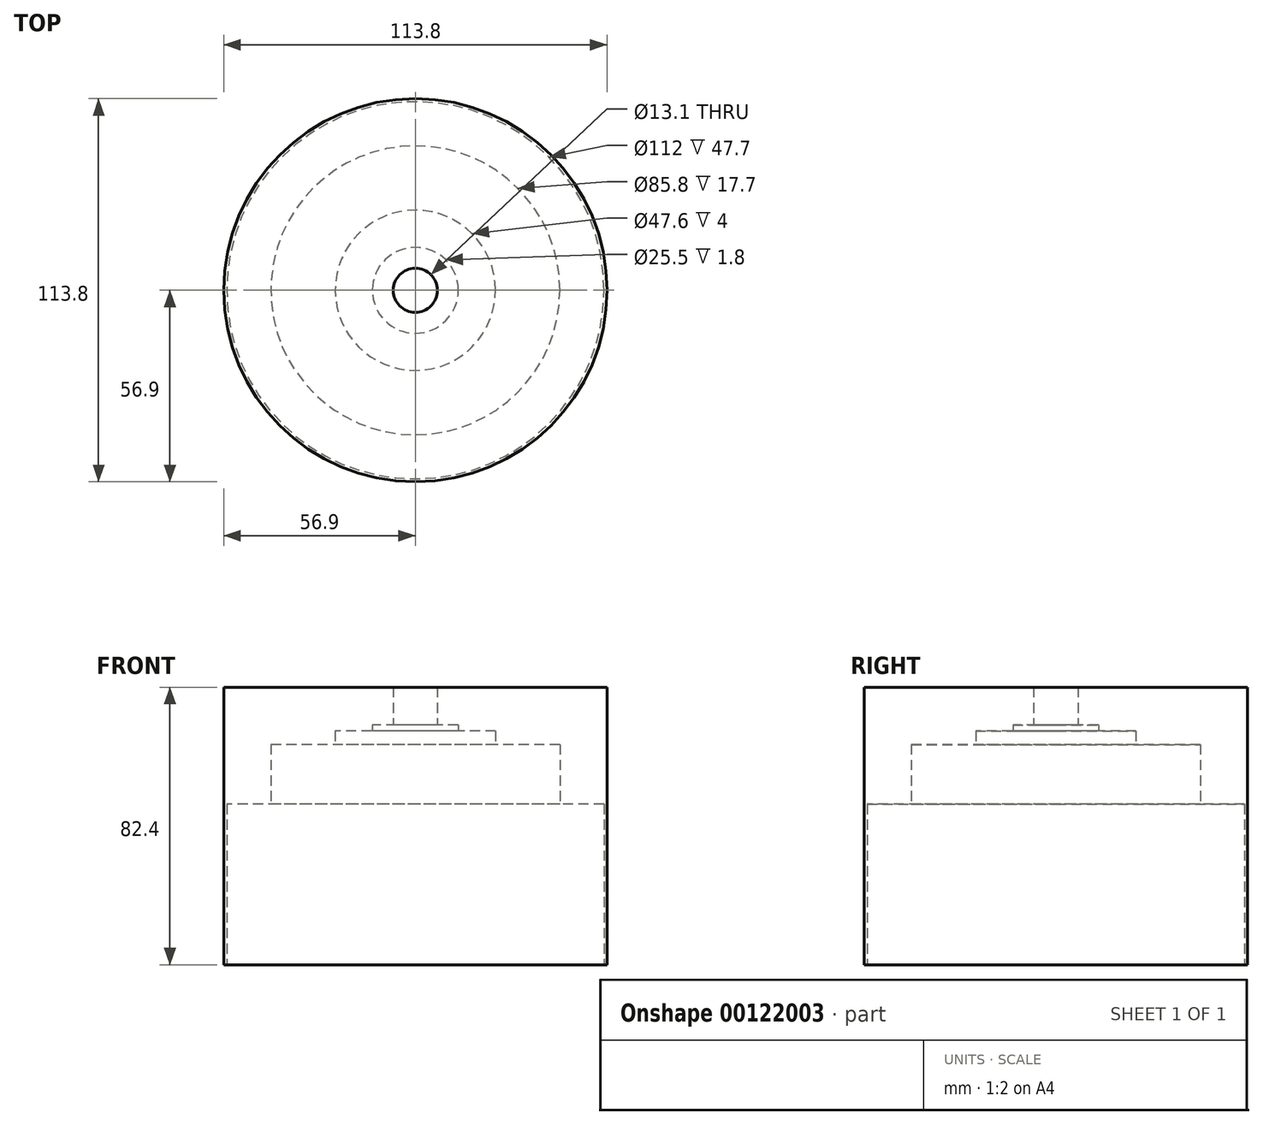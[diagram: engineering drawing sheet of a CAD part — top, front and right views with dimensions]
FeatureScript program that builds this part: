
annotation { "Feature Type Name" : "Feature", "Feature Type Description" : "" }
export const myFeature = defineFeature(function(context is Context, id is Id, definition is map)
    precondition{}
    {
        {
            var Q0;
            Q0=qCreatedBy(makeId("Top.planeOp"),FACE);
            var sketch = newSketch(context, id + "F0", { "sketchPlane" : qUnion([Q0])});
            skCircle(sketch, "E0", {"center": v(0, 0) * mm, "radius": 56.9 * mm});
            skSolve(sketch);
        }
        {
            var Q0;
            Q0=makeQuery(id+"F0.imprint","IMPRINT",FACE,{"disambiguationData":[TD([[makeQuery(id+"F0.imprint","IMPRINT",EDGE,{"derivedFrom":sQuery(id+"F0.wireOp",EDGE,"E0")}),1.0]])]});
            extrude(context, id + "F1", {"entities" : qUnion([Q0]), "depth" : 82.4 * mm});
        }
        {
            var Q0;
            Q0=qCreatedBy(makeId("Top.planeOp"),FACE);
            var sketch = newSketch(context, id + "F2", { "sketchPlane" : qUnion([Q0])});
            skCircle(sketch, "E1", {"center": v(0, 0) * mm, "radius": 6.55 * mm});
            skSolve(sketch);
        }
        {
            var Q0;
            Q0=makeQuery(id+"F2.imprint","IMPRINT",FACE,{"disambiguationData":[TD([[makeQuery(id+"F2.imprint","IMPRINT",EDGE,{"derivedFrom":sQuery(id+"F2.wireOp",EDGE,"E1")}),1.0]])]});
            extrude(context, id + "F3", {"entities" : qUnion([Q0]), "operationType" : NewBodyOperationType.REMOVE, "depth" : 82.4 * mm});
        }
        {
            var Q0;
            Q0=qCreatedBy(makeId("Top.planeOp"),FACE);
            var sketch = newSketch(context, id + "F4", { "sketchPlane" : qUnion([Q0])});
            skCircle(sketch, "E2", {"center": v(0, 0) * mm, "radius": 56 * mm});
            skSolve(sketch);
        }
        {
            var Q0;
            Q0=makeQuery(id+"F4.imprint","IMPRINT",FACE,{"disambiguationData":[TD([[makeQuery(id+"F4.imprint","IMPRINT",EDGE,{"derivedFrom":sQuery(id+"F4.wireOp",EDGE,"E2")}),1.0]])]});
            var Q1;
            Q1=sQuery(id+"F4.wireOp",EDGE,"E2");
            extrude(context, id + "F5", {"entities" : qUnion([Q0]), "operationType" : NewBodyOperationType.REMOVE, "surfaceEntities" : qUnion([Q1]), "depth" : 47.7 * mm});
        }
        {
            var Q0;
            Q0=qCreatedBy(makeId("Top.planeOp"),FACE);
            var sketch = newSketch(context, id + "F6", { "sketchPlane" : qUnion([Q0])});
            skCircle(sketch, "E3", {"center": v(0, 0) * mm, "radius": 42.9 * mm});
            skSolve(sketch);
        }
        {
            var Q0;
            Q0=makeQuery(id+"F6.imprint","IMPRINT",FACE,{"disambiguationData":[TD([[makeQuery(id+"F6.imprint","IMPRINT",EDGE,{"derivedFrom":sQuery(id+"F6.wireOp",EDGE,"E3")}),1.0]])]});
            var Q1;
            Q1=sQuery(id+"F6.wireOp",EDGE,"E3");
            extrude(context, id + "F7", {"entities" : qUnion([Q0]), "operationType" : NewBodyOperationType.REMOVE, "surfaceEntities" : qUnion([Q1]), "depth" : 65.4 * mm});
        }
        {
            var Q0;
            Q0=qCreatedBy(makeId("Top.planeOp"),FACE);
            var sketch = newSketch(context, id + "F8", { "sketchPlane" : qUnion([Q0])});
            skCircle(sketch, "E4", {"center": v(0, 0) * mm, "radius": 23.8 * mm});
            skSolve(sketch);
        }
        {
            var Q0;
            Q0=makeQuery(id+"F8.imprint","IMPRINT",FACE,{"disambiguationData":[TD([[makeQuery(id+"F8.imprint","IMPRINT",EDGE,{"derivedFrom":sQuery(id+"F8.wireOp",EDGE,"E4")}),1.0]])]});
            var Q1;
            Q1=sQuery(id+"F8.wireOp",EDGE,"E4");
            extrude(context, id + "F9", {"entities" : qUnion([Q0]), "operationType" : NewBodyOperationType.REMOVE, "surfaceEntities" : qUnion([Q1]), "depth" : 69.4 * mm});
        }
        {
            var Q0;
            Q0=qCreatedBy(makeId("Top.planeOp"),FACE);
            var sketch = newSketch(context, id + "F10", { "sketchPlane" : qUnion([Q0])});
            skCircle(sketch, "E5", {"center": v(0, 0) * mm, "radius": 12.75 * mm});
            skSolve(sketch);
        }
        {
            var Q0;
            Q0=makeQuery(id+"F10.imprint","IMPRINT",FACE,{"disambiguationData":[TD([[makeQuery(id+"F10.imprint","IMPRINT",EDGE,{"derivedFrom":sQuery(id+"F10.wireOp",EDGE,"E5")}),1.0]])]});
            var Q1;
            Q1=sQuery(id+"F10.wireOp",EDGE,"E5");
            extrude(context, id + "F11", {"entities" : qUnion([Q0]), "operationType" : NewBodyOperationType.REMOVE, "surfaceEntities" : qUnion([Q1]), "depth" : 71.2 * mm});
        }
    });
